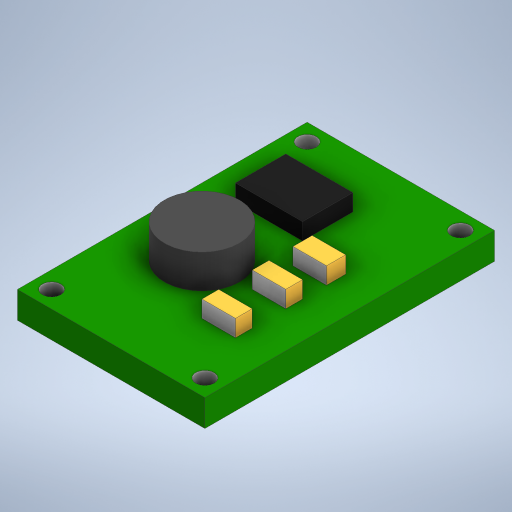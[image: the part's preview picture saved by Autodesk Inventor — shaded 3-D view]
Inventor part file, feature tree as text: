
AUTODESK INVENTOR PART (.ipt)
format: ipt  version: 2023 (Build 270158000, 158)  size: 297,472 bytes
history: native  units: mm
features: extrude x4, sketch x3, other x1, projected_geometry x1
ambient origin geometry x8: Origin, YZ Plane, XZ Plane, XY Plane, X Axis, Y Axis, Z Axis, Center Point
bodies: Body1 (feature_tree)
feature tree (9):
  other  "Bryła1"
  extrude  "Wyciągnięcie proste1"  Depth=17.272mm
  extrude  "Wyciągnięcie proste2"  Depth=11.176mm
  sketch  "Szkic3"
  extrude  "Wyciągnięcie proste3"  Depth=1.6mm TaperAngle=0.0deg
  extrude  "Wyciągnięcie proste4"  Depth=1.1mm
  sketch  "Szkic1"
  sketch  "Szkic2"
  projected_geometry  "Pętla rzutowana1"
